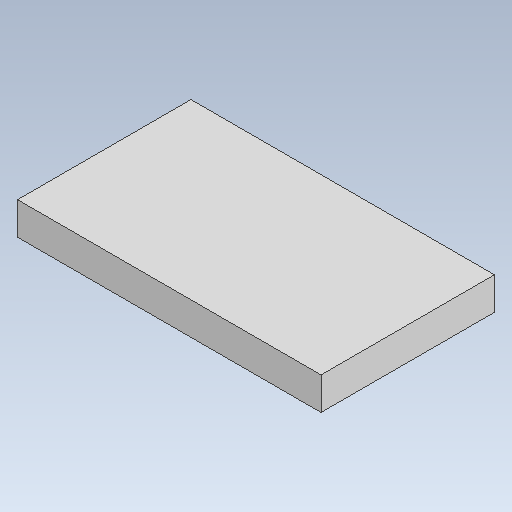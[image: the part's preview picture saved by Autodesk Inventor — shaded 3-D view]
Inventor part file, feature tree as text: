
AUTODESK INVENTOR PART (.ipt)
format: ipt  version: 2021 (Build 250183000, 183)  size: 94,208 bytes
history: native  units: in
note: dims shown in document units (in); Inventor stores cm internally (conversion verified against a paired STEP export)
features: other x5, reference x3, plane x1, extrude x1, sketch x1
ambient origin geometry x8: Origin, YZ Plane, XZ Plane, XY Plane, X Axis, Y Axis, Z Axis, Center Point
bodies: Solid1 (feature_tree)
feature tree (11):
  plane  "Work Plane1"
  extrude  "Extrusion1"  Depth=4.0in TaperAngle=0.0deg
  sketch  "Sketch1"  dims[d0=0.75in d1=4.0in d2=0.0in]
  reference  "Reference1"
  reference  "Reference2"
  reference  "Reference3"
  parser-record x1  (decoder bookkeeping rows leaked as tree rows — omitted from the tree; the rows remain in map.json)
  other  "woodForkAssembly.iam"
  other  "woodForAssemblyLeftSide:1"
  other  "woodForkSupportBase:1"
  other  "woodForAssemblyLeftSide_MIR:1"
note: 1 file-system path scrubbed to <path> (originals preserved in map.json)
